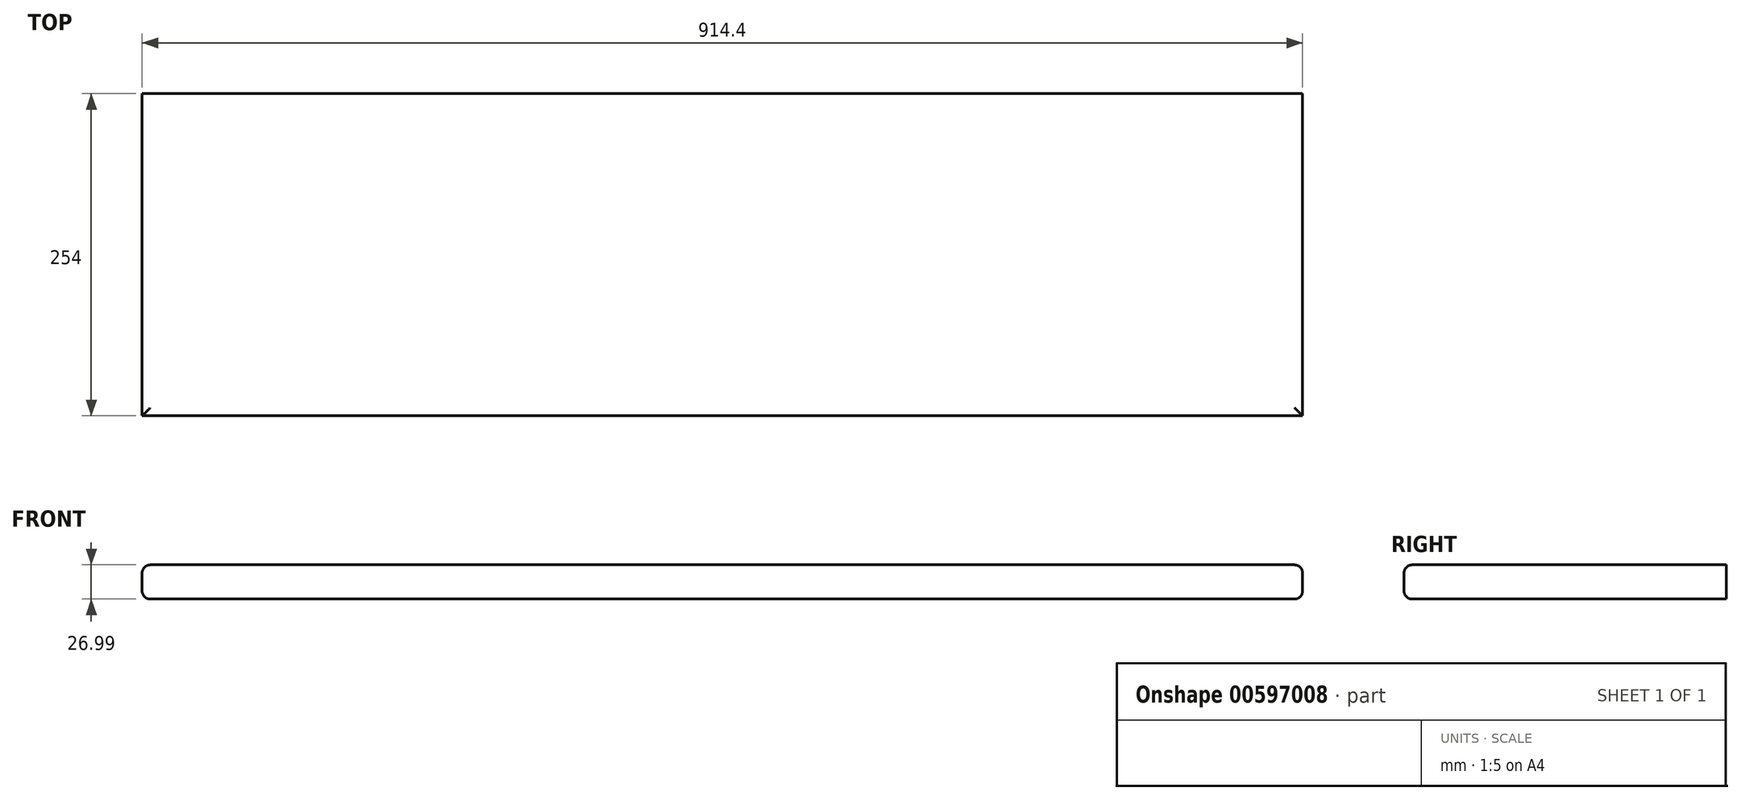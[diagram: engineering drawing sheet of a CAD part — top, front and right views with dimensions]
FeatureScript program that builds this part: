
annotation { "Feature Type Name" : "Feature", "Feature Type Description" : "" }
export const myFeature = defineFeature(function(context is Context, id is Id, definition is map)
    precondition{}
    {
        {
            var Q0;
            Q0=qCreatedBy(makeId("Top.planeOp"),FACE);
            var sketch = newSketch(context, id + "F0", { "sketchPlane" : qUnion([Q0])});
            skLineSegment(sketch, "E0.bottom", {"start": v(-457.2, -25.4) * mm, "end": v(457.2, -25.4) * mm});
            skLineSegment(sketch, "E0.top", {"start": v(-457.2, 228.6) * mm, "end": v(457.2, 228.6) * mm});
            skLineSegment(sketch, "E0.left", {"start": v(-457.2, -25.4) * mm, "end": v(-457.2, 228.6) * mm});
            skLineSegment(sketch, "E0.right", {"start": v(457.2, -25.4) * mm, "end": v(457.2, 228.6) * mm});
            skLineSegment(sketch, "E1", {"start": v(-457.2, 0) * mm, "end": v(457.2, 0) * mm, "construction": true});
            skSolve(sketch);
        }
        {
            var Q0;
            Q0 = qSketchRegion(id + "F0", true);
            extrude(context, id + "F1", {"entities" : qUnion([Q0]), "depth" : 26.99 * mm, "offsetDistance" : 25.4 * mm});
        }
        {
            var Q0;
            Q0=makeQuery(id+"F1.opExtrude","CAP_EDGE",EDGE,{"disambiguationData":[OSD([sQuery(id+"F0.wireOp",EDGE,"E0.bottom")])],"isStart":false});
            var Q1;
            Q1=makeQuery(id+"F1.opExtrude","CAP_EDGE",EDGE,{"disambiguationData":[OSD([sQuery(id+"F0.wireOp",EDGE,"E0.bottom")])],"isStart":true});
            fillet(context, id + "F2", {"entities" : qUnion([Q0, Q1]), "radius" : 6.35 * mm, "tangentPropagation" : true, "allowEdgeOverflow" : false});
        }
        {
            var Q0;
            Q0=makeQuery(id+"F1.opExtrude","CAP_EDGE",EDGE,{"disambiguationData":[OSD([sQuery(id+"F0.wireOp",EDGE,"E0.right")])],"isStart":false});
            var Q1;
            Q1=makeQuery(id+"F1.opExtrude","CAP_EDGE",EDGE,{"disambiguationData":[OSD([sQuery(id+"F0.wireOp",EDGE,"E0.right")])],"isStart":true});
            fillet(context, id + "F3", {"entities" : qUnion([Q0, Q1]), "radius" : 6.35 * mm, "allowEdgeOverflow" : false});
        }
        {
            var Q0;
            Q0=makeQuery(id+"F1.opExtrude","CAP_EDGE",EDGE,{"disambiguationData":[OSD([sQuery(id+"F0.wireOp",EDGE,"E0.left")])],"isStart":true});
            var Q1;
            Q1=makeQuery(id+"F1.opExtrude","CAP_EDGE",EDGE,{"disambiguationData":[OSD([sQuery(id+"F0.wireOp",EDGE,"E0.left")])],"isStart":false});
            fillet(context, id + "F4", {"entities" : qUnion([Q0, Q1]), "radius" : 6.35 * mm, "allowEdgeOverflow" : false});
        }
    });
